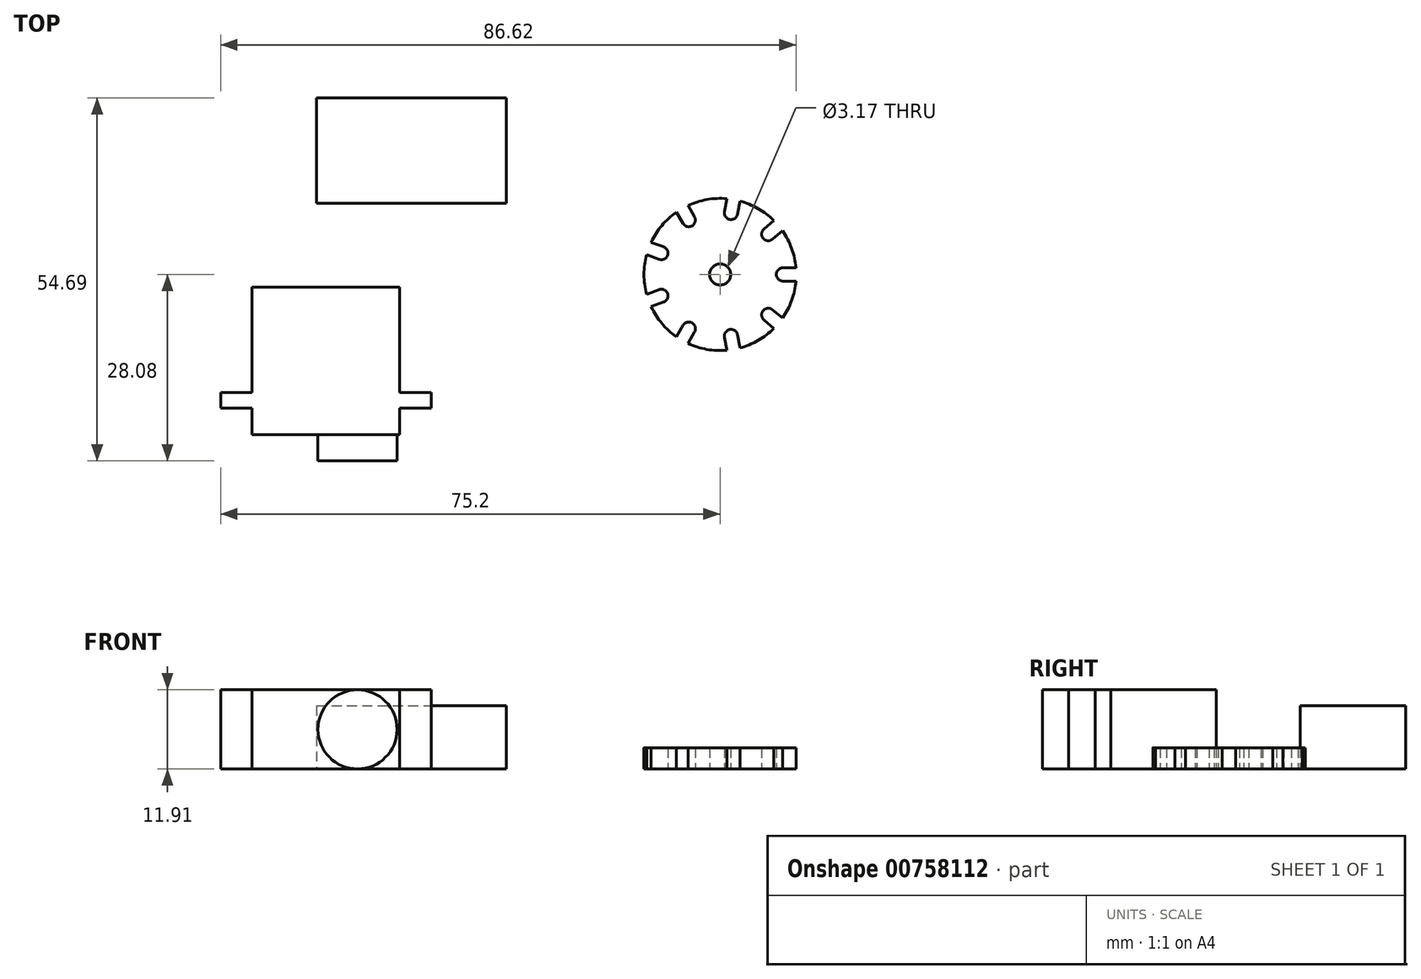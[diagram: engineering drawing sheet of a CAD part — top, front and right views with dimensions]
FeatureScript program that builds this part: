
annotation { "Feature Type Name" : "Feature", "Feature Type Description" : "" }
export const myFeature = defineFeature(function(context is Context, id is Id, definition is map)
    precondition{}
    {
        {
            var Q0;
            Q0=qCreatedBy(makeId("Top.planeOp"),FACE);
            var sketch = newSketch(context, id + "F0", { "sketchPlane" : qUnion([Q0])});
            skCircle(sketch, "E0", {"center": v(0, 0) * mm, "radius": 11.46 * mm});
            skLineSegment(sketch, "E1", {"start": v(0, 0) * mm, "end": v(1.99, 11.29) * mm, "construction": true});
            skLineSegment(sketch, "E2", {"start": v(0, 0) * mm, "end": v(11.46, 0) * mm, "construction": true});
            skLineSegment(sketch, "E3", {"start": v(0, 0) * mm, "end": v(1.99, -11.29) * mm});
            skLineSegment(sketch, "E4", {"start": v(0, 0) * mm, "end": v(-10.77, -3.92) * mm});
            skLineSegment(sketch, "E5", {"start": v(0, 0) * mm, "end": v(-10.77, 3.92) * mm});
            skLineSegment(sketch, "E6", {"start": v(0, 0) * mm, "end": v(-5.73, 9.92) * mm});
            skLineSegment(sketch, "E7", {"start": v(0, 0) * mm, "end": v(8.78, 7.37) * mm});
            skLineSegment(sketch, "E8", {"start": v(0, 0) * mm, "end": v(8.78, -7.37) * mm});
            skLineSegment(sketch, "E9", {"start": v(0, 0) * mm, "end": v(-5.73, -9.92) * mm});
            skPoint(sketch, "E10", {"position": v(7.25, 6.08) * mm});
            skCircle(sketch, "E11", {"center": v(7.25, 6.08) * mm, "radius": 1 * mm});
            skLineSegment(sketch, "E12", {"start": v(6.6, 6.85) * mm, "end": v(8.1, 8.1) * mm});
            skLineSegment(sketch, "E13", {"start": v(7.89, 5.31) * mm, "end": v(9.39, 6.57) * mm});
            skPoint(sketch, "E14", {"position": v(1.63, 9.27) * mm});
            skPoint(sketch, "E15", {"position": v(-4.73, 8.2) * mm});
            skCircle(sketch, "E16", {"center": v(1.63, 9.27) * mm, "radius": 1 * mm});
            skCircle(sketch, "E17", {"center": v(-4.73, 8.2) * mm, "radius": 1 * mm});
            skLineSegment(sketch, "E18", {"start": v(0.65, 9.45) * mm, "end": v(1, 11.42) * mm});
            skLineSegment(sketch, "E19", {"start": v(2.62, 9.1) * mm, "end": v(2.97, 11.07) * mm});
            skLineSegment(sketch, "E20", {"start": v(0.65, 9.45) * mm, "end": v(2.62, 9.1) * mm, "construction": true});
            skLineSegment(sketch, "E21", {"start": v(-3.86, 8.7) * mm, "end": v(-4.84, 10.39) * mm});
            skLineSegment(sketch, "E22", {"start": v(-5.6, 7.7) * mm, "end": v(-6.57, 9.39) * mm});
            skPoint(sketch, "E23", {"position": v(-8.85, 3.22) * mm});
            skPoint(sketch, "E24", {"position": v(-8.85, -3.22) * mm});
            skPoint(sketch, "E25", {"position": v(-4.7, -8.15) * mm});
            skPoint(sketch, "E26", {"position": v(1.63, -9.27) * mm});
            skPoint(sketch, "E27", {"position": v(7.25, -6.08) * mm});
            skPoint(sketch, "E28", {"position": v(9.46, 0) * mm});
            skCircle(sketch, "E29", {"center": v(-8.85, 3.22) * mm, "radius": 1 * mm});
            skCircle(sketch, "E30", {"center": v(-8.85, -3.22) * mm, "radius": 1 * mm});
            skCircle(sketch, "E31", {"center": v(-4.7, -8.15) * mm, "radius": 1 * mm});
            skCircle(sketch, "E32", {"center": v(1.63, -9.27) * mm, "radius": 1 * mm});
            skCircle(sketch, "E33", {"center": v(7.25, -6.08) * mm, "radius": 1 * mm});
            skCircle(sketch, "E34", {"center": v(9.46, 0) * mm, "radius": 1 * mm});
            skLineSegment(sketch, "E35", {"start": v(-8.5, 4.16) * mm, "end": v(-10.38, 4.84) * mm});
            skLineSegment(sketch, "E36", {"start": v(-9.19, 2.28) * mm, "end": v(-11.07, 2.96) * mm});
            skLineSegment(sketch, "E37", {"start": v(-9.19, -2.28) * mm, "end": v(-11.07, -2.96) * mm});
            skLineSegment(sketch, "E38", {"start": v(-8.5, -4.16) * mm, "end": v(-10.38, -4.84) * mm});
            skLineSegment(sketch, "E39", {"start": v(-5.57, -7.65) * mm, "end": v(-6.57, -9.39) * mm});
            skLineSegment(sketch, "E40", {"start": v(-3.84, -8.65) * mm, "end": v(-4.84, -10.39) * mm});
            skLineSegment(sketch, "E41", {"start": v(9.46, 1) * mm, "end": v(11.42, 1) * mm});
            skLineSegment(sketch, "E42", {"start": v(9.46, -1) * mm, "end": v(11.42, -1) * mm});
            skLineSegment(sketch, "E43", {"start": v(6.6, -6.85) * mm, "end": v(8.1, -8.1) * mm});
            skLineSegment(sketch, "E44", {"start": v(7.89, -5.31) * mm, "end": v(9.39, -6.57) * mm});
            skLineSegment(sketch, "E45", {"start": v(2.62, -9.1) * mm, "end": v(2.97, -11.07) * mm});
            skLineSegment(sketch, "E46", {"start": v(0.65, -9.45) * mm, "end": v(1, -11.42) * mm});
            skLineSegment(sketch, "E47", {"start": v(0.65, -9.45) * mm, "end": v(2.62, -9.1) * mm, "construction": true});
            skCircle(sketch, "E48", {"center": v(0, 0) * mm, "radius": 1.59 * mm});
            skSolve(sketch);
        }
        {
            var Q0;
            {var subQ0=sQuery(id+"F0.wireOp",EDGE,"E12");Q0=makeQuery(id+"F0.imprint","IMPRINT",FACE,{"disambiguationData":[TD([[makeQuery(id+"F0.imprint","IMPRINT",EDGE,{"derivedFrom":subQ0}),1.0]])]});}
            var Q1;
            {var subQ3=sQuery(id+"F0.wireOp",EDGE,"E13");Q1=makeQuery(id+"F0.imprint","IMPRINT",FACE,{"disambiguationData":[TD([[makeQuery(id+"F0.imprint","IMPRINT",EDGE,{"derivedFrom":subQ3}),-1.0]])]});}
            var Q2;
            {var subQ8=sQuery(id+"F0.wireOp",EDGE,"E43");Q2=makeQuery(id+"F0.imprint","IMPRINT",FACE,{"disambiguationData":[TD([[makeQuery(id+"F0.imprint","IMPRINT",EDGE,{"derivedFrom":subQ8}),-1.0]])]});}
            var Q3;
            {var subQ0=sQuery(id+"F0.wireOp",EDGE,"E40");Q3=makeQuery(id+"F0.imprint","IMPRINT",FACE,{"disambiguationData":[TD([[makeQuery(id+"F0.imprint","IMPRINT",EDGE,{"derivedFrom":subQ0}),1.0]])]});}
            var Q4;
            {var subQ5=sQuery(id+"F0.wireOp",EDGE,"E38");Q4=makeQuery(id+"F0.imprint","IMPRINT",FACE,{"disambiguationData":[TD([[makeQuery(id+"F0.imprint","IMPRINT",EDGE,{"derivedFrom":subQ5}),1.0]])]});}
            var Q5;
            {var subQ0=sQuery(id+"F0.wireOp",EDGE,"E36");Q5=makeQuery(id+"F0.imprint","IMPRINT",FACE,{"disambiguationData":[TD([[makeQuery(id+"F0.imprint","IMPRINT",EDGE,{"derivedFrom":subQ0}),1.0]])]});}
            var Q6;
            {var subQ5=sQuery(id+"F0.wireOp",EDGE,"E22");Q6=makeQuery(id+"F0.imprint","IMPRINT",FACE,{"disambiguationData":[TD([[makeQuery(id+"F0.imprint","IMPRINT",EDGE,{"derivedFrom":subQ5}),1.0]])]});}
            extrude(context, id + "F1", {"entities" : qUnion([Q0, Q1, Q2, Q3, Q4, Q5, Q6]), "depth" : 3.17 * mm, "offsetDistance" : 25.4 * mm});
        }
        {
            var Q0;
            Q0=qCreatedBy(makeId("Top.planeOp"),FACE);
            var sketch = newSketch(context, id + "F2", { "sketchPlane" : qUnion([Q0])});
            skLineSegment(sketch, "E49.bottom", {"start": v(-70.45, -1.9) * mm, "end": v(-48.23, -1.9) * mm});
            skLineSegment(sketch, "E49.top", {"start": v(-70.45, -24.12) * mm, "end": v(-48.23, -24.12) * mm});
            skLineSegment(sketch, "E49.left", {"start": v(-70.45, -1.9) * mm, "end": v(-70.45, -24.12) * mm});
            skLineSegment(sketch, "E49.right", {"start": v(-48.23, -1.9) * mm, "end": v(-48.23, -24.12) * mm});
            skLineSegment(sketch, "E50.bottom", {"start": v(-70.45, -17.77) * mm, "end": v(-75.2, -17.77) * mm});
            skLineSegment(sketch, "E50.top", {"start": v(-70.45, -20.15) * mm, "end": v(-75.2, -20.15) * mm});
            skLineSegment(sketch, "E50.left", {"start": v(-70.45, -17.77) * mm, "end": v(-70.45, -20.15) * mm});
            skLineSegment(sketch, "E50.right", {"start": v(-75.2, -17.77) * mm, "end": v(-75.2, -20.15) * mm});
            skLineSegment(sketch, "E51", {"start": v(-59.34, -1.9) * mm, "end": v(-59.34, -24.12) * mm, "construction": true});
            skLineSegment(sketch, "E52.MirrorCS", {"start": v(-48.23, -17.77) * mm, "end": v(-43.48, -17.77) * mm});
            skLineSegment(sketch, "E53.MirrorCS", {"start": v(-43.48, -17.77) * mm, "end": v(-43.48, -20.15) * mm});
            skLineSegment(sketch, "E54.MirrorCS", {"start": v(-48.23, -20.15) * mm, "end": v(-43.48, -20.15) * mm});
            skSolve(sketch);
        }
        {
            var Q0;
            {var subQ3=sQuery(id+"F2.wireOp",EDGE,"E49.bottom");Q0=makeQuery(id+"F2.imprint","IMPRINT",FACE,{"disambiguationData":[TD([[makeQuery(id+"F2.imprint","IMPRINT",EDGE,{"derivedFrom":subQ3}),-1.0]])]});}
            var Q1;
            Q1=makeQuery(id+"F2.imprint","IMPRINT",FACE,{"disambiguationData":[TD([[makeQuery(id+"F2.imprint","IMPRINT",EDGE,{"derivedFrom":sQuery(id+"F2.wireOp",EDGE,"E50.bottom")}),1.0]])]});
            var Q2;
            {var subQ0=sQuery(id+"F2.wireOp",EDGE,"E52.MirrorCS");Q2=makeQuery(id+"F2.imprint","IMPRINT",FACE,{"disambiguationData":[TD([[makeQuery(id+"F2.imprint","IMPRINT",EDGE,{"derivedFrom":subQ0}),-1.0]])]});}
            extrude(context, id + "F3", {"entities" : qUnion([Q0, Q1, Q2]), "depth" : 11.9 * mm, "offsetDistance" : 25.4 * mm});
        }
        {
            var Q0;
            Q0=makeQuery(id+"F3.opExtrude","SWEPT_FACE",FACE,{"disambiguationData":[OSD([sQuery(id+"F2.wireOp",EDGE,"E49.top")])]});
            var sketch = newSketch(context, id + "F4", { "sketchPlane" : qUnion([Q0])});
            skCircle(sketch, "E55", {"center": v(-54.59, 5.96) * mm, "radius": 5.96 * mm});
            skSolve(sketch);
        }
        {
            var Q0;
            {var subQ0=sQuery(id+"F4.wireOp",EDGE,"E55");var subQ1=sQuery(id+"F2.wireOp",EDGE,"E49.top");var subQ2=makeQuery(id+"F4.imprint","INTERSECT",VERTEX,{"derivedFrom":[makeQuery(id+"F3.opExtrude","CAP_EDGE",EDGE,{"disambiguationData":[OSD([subQ1])],"isStart":true}),subQ0]});Q0=makeQuery(id+"F4.imprint","IMPRINT",FACE,{"disambiguationData":[TD([[makeQuery(id+"F4.imprint","IMPRINT",EDGE,{"disambiguationData":[TD([[subQ2,1.0]])],"derivedFrom":subQ0}),1.0]])]});}
            extrude(context, id + "F5", {"entities" : qUnion([Q0]), "operationType" : NewBodyOperationType.ADD, "depth" : 3.96 * mm, "offsetDistance" : 25.4 * mm});
        }
        {
            var Q0;
            Q0=qCreatedBy(makeId("Top.planeOp"),FACE);
            var sketch = newSketch(context, id + "F6", { "sketchPlane" : qUnion([Q0])});
            skLineSegment(sketch, "E56.bottom", {"start": v(-60.76, 26.61) * mm, "end": v(-32.18, 26.61) * mm});
            skLineSegment(sketch, "E56.top", {"start": v(-60.76, 10.74) * mm, "end": v(-32.18, 10.74) * mm});
            skLineSegment(sketch, "E56.left", {"start": v(-60.76, 26.61) * mm, "end": v(-60.76, 10.74) * mm});
            skLineSegment(sketch, "E56.right", {"start": v(-32.18, 26.61) * mm, "end": v(-32.18, 10.74) * mm});
            skSolve(sketch);
        }
        {
            var Q0;
            Q0=makeQuery(id+"F6.imprint","IMPRINT",FACE,{"disambiguationData":[TD([[makeQuery(id+"F6.imprint","IMPRINT",EDGE,{"derivedFrom":sQuery(id+"F6.wireOp",EDGE,"E56.bottom")}),-1.0]])]});
            extrude(context, id + "F7", {"entities" : qUnion([Q0]), "depth" : 9.52 * mm, "offsetDistance" : 25.4 * mm});
        }
    });
